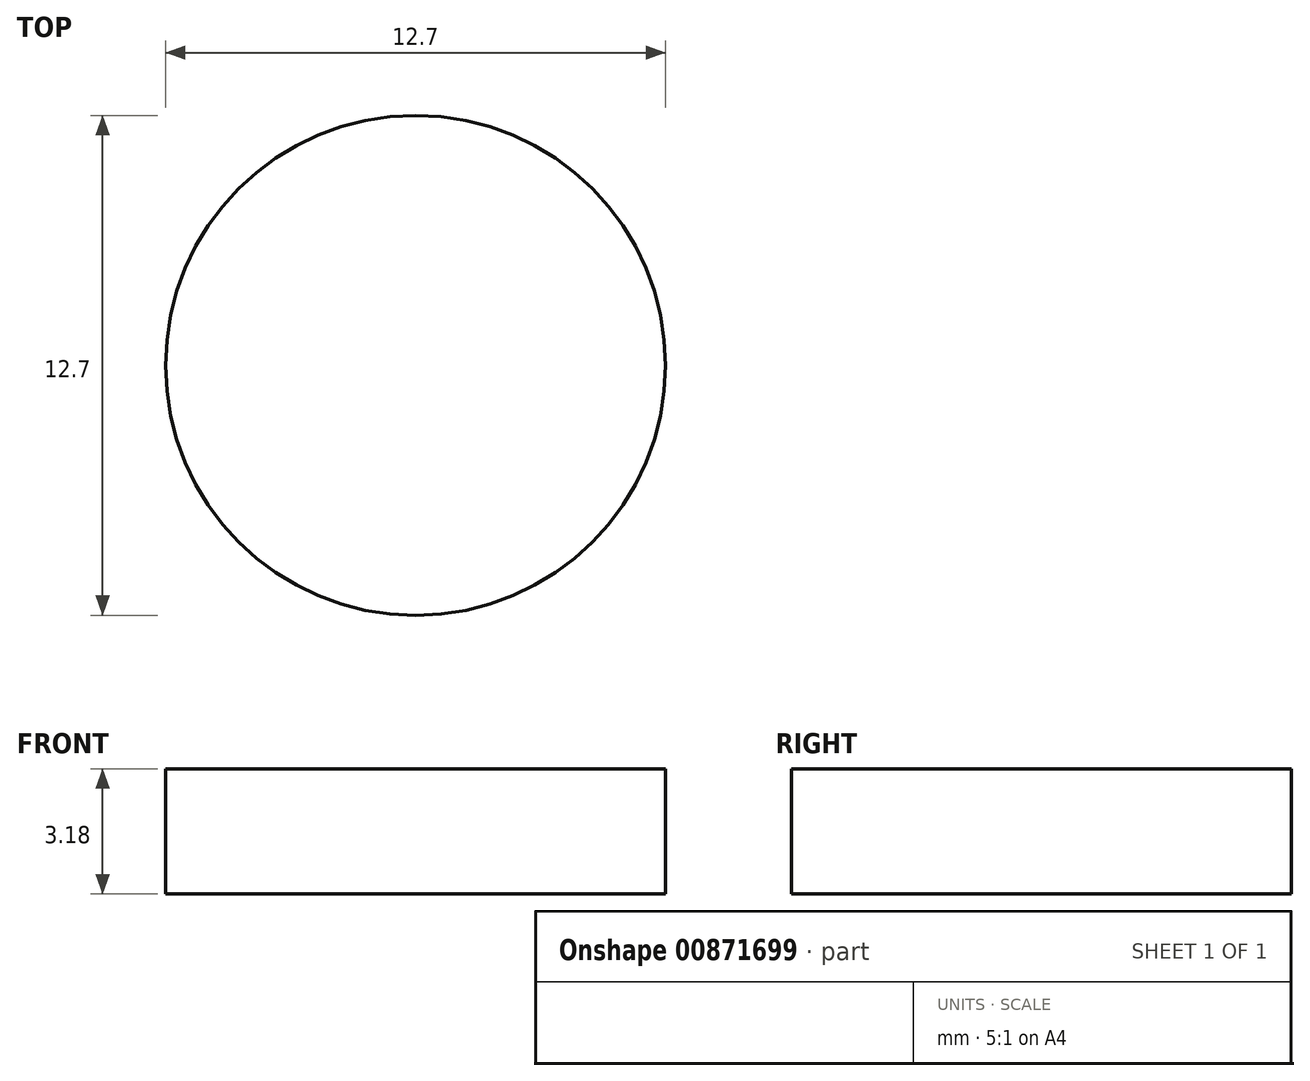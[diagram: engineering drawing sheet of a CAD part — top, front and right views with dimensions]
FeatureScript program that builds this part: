
annotation { "Feature Type Name" : "Feature", "Feature Type Description" : "" }
export const myFeature = defineFeature(function(context is Context, id is Id, definition is map)
    precondition{}
    {
        {
            var Q0;
            Q0=qCreatedBy(makeId("Top.planeOp"),FACE);
            var sketch = newSketch(context, id + "F0", { "sketchPlane" : qUnion([Q0])});
            skCircle(sketch, "E0", {"center": v(0, 0) * mm, "radius": 6.35 * mm});
            skSolve(sketch);
        }
        {
            var Q0;
            Q0 = qSketchRegion(id + "F0", true);
            extrude(context, id + "F1", {"entities" : qUnion([Q0]), "depth" : 3.17 * mm, "offsetDistance" : 25.4 * mm});
        }
    });
